# Revit family: FONESTAR_Altavoz_Sonorización
name_source: partatom
category: Dispositivos de comunicación
units: mm (PartAtom-declared; Revit-internal decimal feet)

## family parameters
Compartido = No
Corte con vacíos al cargar = No
Cota de conector redondo = Diámetro de uso
Mantener orientación de anotación = No
Punto de cálculo de habitación = No
Se basa en plano de trabajo = Sí
Siempre vertical = No
Tipo de pieza = Normal

## types (1)
- FONESTAR_Altavoz_Sonorización
    Anchura = 125 mm  [stored 0.410105 ft]
    Brazo.Longitud = 60 mm  [stored 0.19685 ft]
    Cuerpo.Espesor = 3 mm  [stored 0.00984252 ft]
    Cuerpo.Material = Plástico ABS - Blanco RAL(9003)
    Cuerpo.Redondeo = 20 mm  [stored 0.0656168 ft]
    Descripción = Altavoz de sonorización con transformador de línea 100 V y baja impedancia. Preparado para uso en exteriores, protección contra agua y materiales anticorrosión.
    Elevación por defecto = 1000 mm  [stored 3.28084 ft]
    Fabricante = FONESTAR
    Longitud = 202 mm  [stored 0.66273 ft]
    Modelo = SONORA-4TB
    Modified by = XPV
    Peso = 1,7 Kg
    Potencia Acústica = 30 W RMS
    Profundidad = 125 mm  [stored 0.410105 ft]
    Protección IP = IP-66
    Rejilla.Material = Aluminio_Rejilla - Blanco RAL(9003)
    Respuesta Acústica = 120-20.000 Hz
    Reviewed by = TAG
    Soporte.Brazo.Material = Plástico ABS - Blanco RAL(9003)
    Soporte.Material = Plástico ABS - Blanco RAL(9003)
    URL = https://fonestar.com
    URL.Product = https://fonestar.com
    Version = R1

note: [stored X ft] marks values corroborated as IEEE doubles in the binary element streams (Revit-internal decimal feet)
